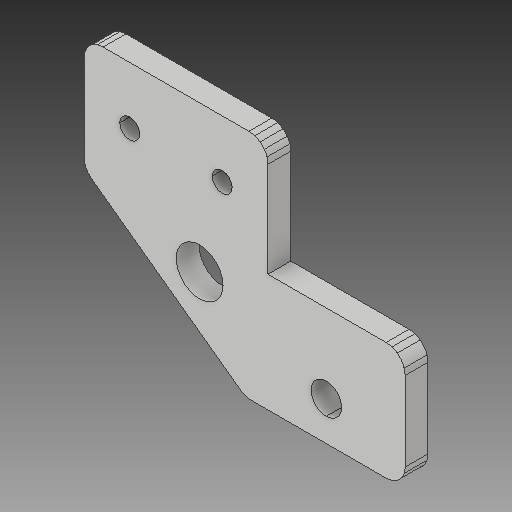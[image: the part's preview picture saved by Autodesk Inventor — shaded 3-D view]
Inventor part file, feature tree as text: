
AUTODESK INVENTOR PART (.ipt)
format: ipt  version: 2018 (Build 220112000, 112)  size: 247,296 bytes
history: native  units: mm
features: other x3, sketch x3, extrude x1
ambient origin geometry x8: Origin, YZ Plane, XZ Plane, XY Plane, X Axis, Y Axis, Z Axis, Center Point
bodies: Solid1 (feature_tree)
feature tree (7):
  other  "Leadscrew-rod-holder.ipt"
  extrude  "Extrusion1"  Depth=10.0mm TaperAngle=0.0deg
  other  "Solid1::Leadscrew-rod-holder.ipt"
  other  "TaggingFeature1"
  sketch  "Sketch1"  dims[d0=10.0mm d1=10.0mm d2=0.0mm]
  sketch  "Sketch2"  dims[d3=12.3mm]
  sketch  "Sketch3"
